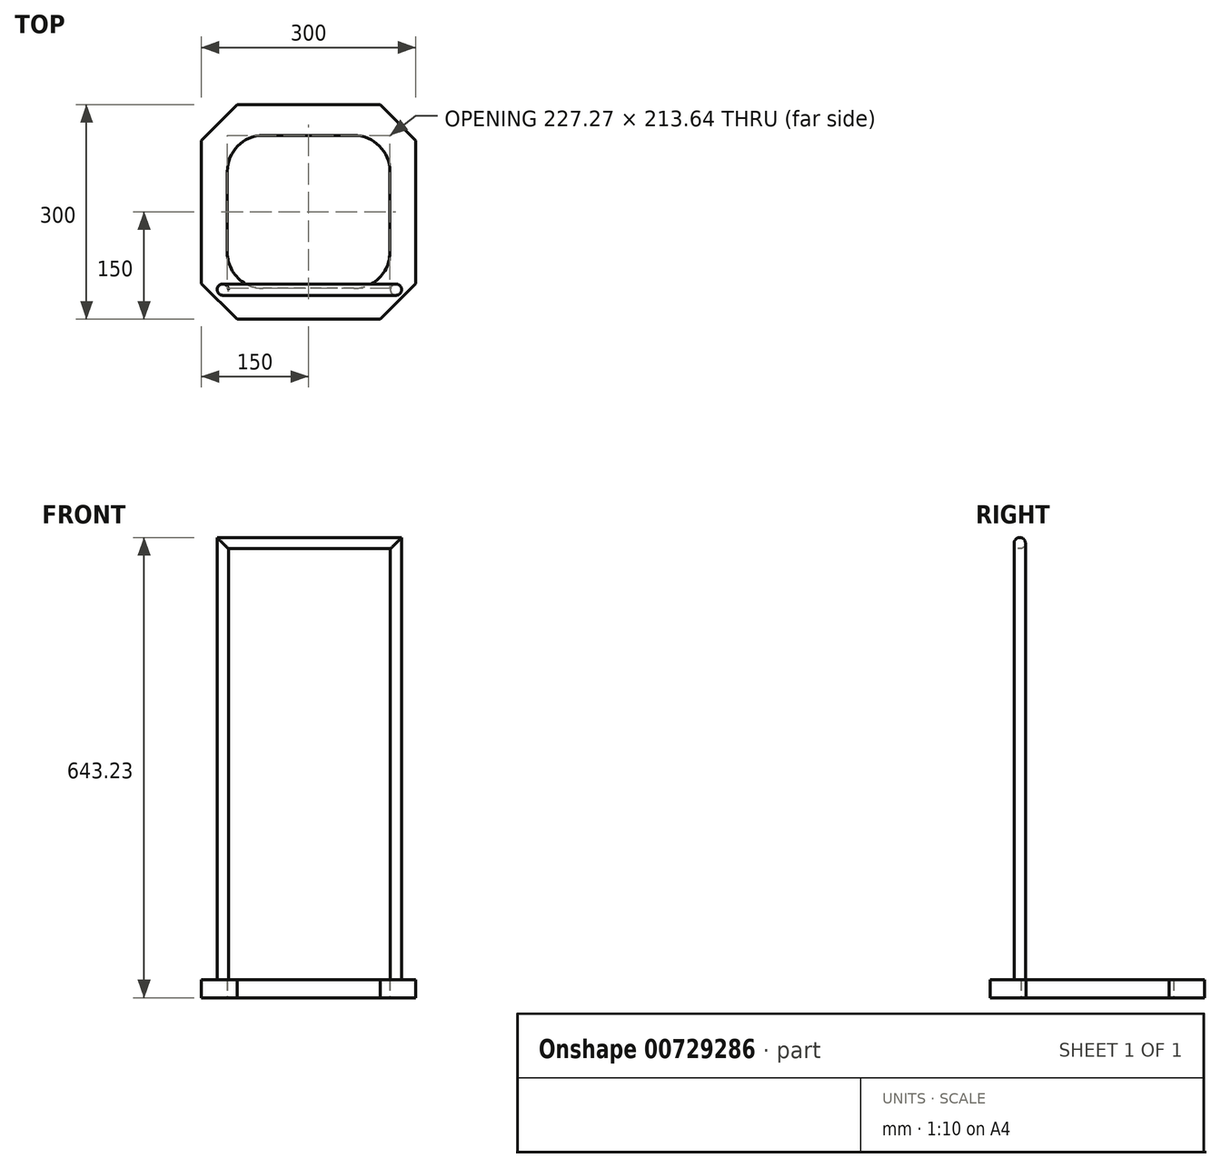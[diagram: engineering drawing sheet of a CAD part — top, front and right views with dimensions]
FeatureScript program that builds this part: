
annotation { "Feature Type Name" : "Feature", "Feature Type Description" : "" }
export const myFeature = defineFeature(function(context is Context, id is Id, definition is map)
    precondition{}
    {
        {
            var Q0;
            Q0=qCreatedBy(makeId("Top.planeOp"),FACE);
            var sketch = newSketch(context, id + "F0", { "sketchPlane" : qUnion([Q0])});
            skLineSegment(sketch, "E0.bottom", {"start": v(150, -150) * mm, "end": v(-150, -150) * mm});
            skLineSegment(sketch, "E0.top", {"start": v(150, 150) * mm, "end": v(-150, 150) * mm});
            skLineSegment(sketch, "E0.left", {"start": v(150, -150) * mm, "end": v(150, 150) * mm});
            skLineSegment(sketch, "E0.right", {"start": v(-150, -150) * mm, "end": v(-150, 150) * mm});
            skPoint(sketch, "E0.middle", {"position": v(0, 0) * mm});
            skLineSegment(sketch, "E1.bottom", {"start": v(113.64, -106.82) * mm, "end": v(-113.64, -106.82) * mm});
            skLineSegment(sketch, "E1.top", {"start": v(113.64, 106.82) * mm, "end": v(-113.64, 106.82) * mm});
            skLineSegment(sketch, "E1.left", {"start": v(113.64, -106.82) * mm, "end": v(113.64, 106.82) * mm});
            skLineSegment(sketch, "E1.right", {"start": v(-113.64, -106.82) * mm, "end": v(-113.64, 106.82) * mm});
            skSolve(sketch);
        }
        {
            var Q0;
            Q0 = qSketchRegion(id + "F0", true);
            extrude(context, id + "F1", {"entities" : qUnion([Q0]), "depth" : 25 * mm, "offsetDistance" : 25 * mm});
        }
        {
            var Q0;
            Q0=makeQuery(id+"F1.opExtrude","SWEPT_EDGE",EDGE,{"disambiguationData":[OSD([sQuery(id+"F0.wireOp",EDGE,"E1.bottom"),sQuery(id+"F0.wireOp",EDGE,"E1.right")])]});
            var Q1;
            Q1=makeQuery(id+"F1.opExtrude","SWEPT_EDGE",EDGE,{"disambiguationData":[OSD([sQuery(id+"F0.wireOp",EDGE,"E1.top"),sQuery(id+"F0.wireOp",EDGE,"E1.right")])]});
            var Q2;
            Q2=makeQuery(id+"F1.opExtrude","SWEPT_EDGE",EDGE,{"disambiguationData":[OSD([sQuery(id+"F0.wireOp",EDGE,"E1.bottom"),sQuery(id+"F0.wireOp",EDGE,"E1.left")])]});
            var Q3;
            Q3=makeQuery(id+"F1.opExtrude","SWEPT_EDGE",EDGE,{"disambiguationData":[OSD([sQuery(id+"F0.wireOp",EDGE,"E1.top"),sQuery(id+"F0.wireOp",EDGE,"E1.left")])]});
            fillet(context, id + "F2", {"entities" : qUnion([Q0, Q1, Q2, Q3]), "radius" : 50 * mm, "tangentPropagation" : true, "allowEdgeOverflow" : false});
        }
        {
            var Q0;
            Q0=makeQuery(id+"F1.opExtrude","SWEPT_EDGE",EDGE,{"disambiguationData":[OSD([sQuery(id+"F0.wireOp",EDGE,"E0.top"),sQuery(id+"F0.wireOp",EDGE,"E0.right")])]});
            var Q1;
            Q1=makeQuery(id+"F1.opExtrude","SWEPT_EDGE",EDGE,{"disambiguationData":[OSD([sQuery(id+"F0.wireOp",EDGE,"E0.top"),sQuery(id+"F0.wireOp",EDGE,"E0.left")])]});
            var Q2;
            Q2=makeQuery(id+"F1.opExtrude","SWEPT_EDGE",EDGE,{"disambiguationData":[OSD([sQuery(id+"F0.wireOp",EDGE,"E0.bottom"),sQuery(id+"F0.wireOp",EDGE,"E0.left")])]});
            var Q3;
            Q3=makeQuery(id+"F1.opExtrude","SWEPT_EDGE",EDGE,{"disambiguationData":[OSD([sQuery(id+"F0.wireOp",EDGE,"E0.bottom"),sQuery(id+"F0.wireOp",EDGE,"E0.right")])]});
            chamfer(context, id + "F3", {"entities" : qUnion([Q0, Q1, Q2, Q3]), "width" : 50 * mm, "tangentPropagation" : true});
        }
        {
            var Q0;
            Q0=makeQuery(id+"F1.opExtrude","SWEPT_FACE",FACE,{"disambiguationData":[OSD([sQuery(id+"F0.wireOp",EDGE,"E0.bottom")])]});
            cPlane(context, id + "F4", {"entities" : qUnion([Q0]), "cplaneType" : CPlaneType.OFFSET, "offset" : 35 * mm, "oppositeDirection" : true, "width" : 150 * mm, "height" : 150 * mm});
        }
        {
            var Q0;
            Q0=qCreatedBy(id+"F4.planeOp",FACE);
            var sketch = newSketch(context, id + "F5", { "sketchPlane" : qUnion([Q0])});
            skLineSegment(sketch, "E2", {"start": v(-124.5, 0) * mm, "end": v(-124.5, 639.9) * mm});
            skLineSegment(sketch, "E3", {"start": v(126.83, 0) * mm, "end": v(126.83, 639.9) * mm});
            skLineSegment(sketch, "E4", {"start": v(126.83, 639.9) * mm, "end": v(-124.5, 639.9) * mm});
            skSolve(sketch);
        }
        {
            var Q0;
            Q0=makeQuery(id+"F1.opExtrude","CAP_FACE",FACE,{"disambiguationData":[OSD([sQuery(id+"F0.wireOp",EDGE,"E0.bottom"),sQuery(id+"F0.wireOp",EDGE,"E0.top"),sQuery(id+"F0.wireOp",EDGE,"E0.left"),sQuery(id+"F0.wireOp",EDGE,"E0.right"),sQuery(id+"F0.wireOp",EDGE,"E1.bottom"),sQuery(id+"F0.wireOp",EDGE,"E1.top"),sQuery(id+"F0.wireOp",EDGE,"E1.left"),sQuery(id+"F0.wireOp",EDGE,"E1.right")])],"isStart":false});
            var sketch = newSketch(context, id + "F6", { "sketchPlane" : qUnion([Q0])});
            skCircle(sketch, "E5", {"center": v(122.28, -108.6) * mm, "radius": 7.88 * mm});
            skSolve(sketch);
        }
        {
            var Q0;
            {var subQ0=sQuery(id+"F6.wireOp",EDGE,"E5");var subQ1=sQuery(id+"F0.wireOp",EDGE,"E0.left");var subQ2=sQuery(id+"F0.wireOp",EDGE,"E0.bottom");var subQ3=makeQuery(id+"F3.opChamfer","BLEND_EDGE",EDGE,{"blendedFrom":[makeQuery(id+"F1.opExtrude","SWEPT_EDGE",EDGE,{"disambiguationData":[OSD([subQ2,subQ1])]}),makeQuery(id+"F1.opExtrude","CAP_FACE",FACE,{"disambiguationData":[OSD([subQ2,sQuery(id+"F0.wireOp",EDGE,"E0.top"),subQ1,sQuery(id+"F0.wireOp",EDGE,"E0.right"),sQuery(id+"F0.wireOp",EDGE,"E1.bottom"),sQuery(id+"F0.wireOp",EDGE,"E1.top"),sQuery(id+"F0.wireOp",EDGE,"E1.left"),sQuery(id+"F0.wireOp",EDGE,"E1.right")])],"isStart":false})],"blendedInto":[makeQuery(id+"F1.opExtrude","CAP_FACE",FACE,{"disambiguationData":[OSD([subQ2,sQuery(id+"F0.wireOp",EDGE,"E0.top"),subQ1,sQuery(id+"F0.wireOp",EDGE,"E0.right"),sQuery(id+"F0.wireOp",EDGE,"E1.bottom"),sQuery(id+"F0.wireOp",EDGE,"E1.top"),sQuery(id+"F0.wireOp",EDGE,"E1.left"),sQuery(id+"F0.wireOp",EDGE,"E1.right")])],"isStart":false})]});var subQ4=makeQuery(id+"F6.imprint","INTERSECT",VERTEX,{"disambiguationData":[OD(0.0)],"derivedFrom":[subQ3,subQ0]});Q0=makeQuery(id+"F6.imprint","IMPRINT",FACE,{"disambiguationData":[TD([[makeQuery(id+"F6.imprint","IMPRINT",EDGE,{"disambiguationData":[TD([[subQ4,-1.0]])],"derivedFrom":subQ0}),1.0]])]});}
            var Q1;
            {var subQ0=sQuery(id+"F6.wireOp",EDGE,"E5");var subQ1=sQuery(id+"F0.wireOp",EDGE,"E0.left");var subQ2=sQuery(id+"F0.wireOp",EDGE,"E0.bottom");var subQ3=makeQuery(id+"F3.opChamfer","BLEND_EDGE",EDGE,{"blendedFrom":[makeQuery(id+"F1.opExtrude","SWEPT_EDGE",EDGE,{"disambiguationData":[OSD([subQ2,subQ1])]}),makeQuery(id+"F1.opExtrude","CAP_FACE",FACE,{"disambiguationData":[OSD([subQ2,sQuery(id+"F0.wireOp",EDGE,"E0.top"),subQ1,sQuery(id+"F0.wireOp",EDGE,"E0.right"),sQuery(id+"F0.wireOp",EDGE,"E1.bottom"),sQuery(id+"F0.wireOp",EDGE,"E1.top"),sQuery(id+"F0.wireOp",EDGE,"E1.left"),sQuery(id+"F0.wireOp",EDGE,"E1.right")])],"isStart":false})],"blendedInto":[makeQuery(id+"F1.opExtrude","CAP_FACE",FACE,{"disambiguationData":[OSD([subQ2,sQuery(id+"F0.wireOp",EDGE,"E0.top"),subQ1,sQuery(id+"F0.wireOp",EDGE,"E0.right"),sQuery(id+"F0.wireOp",EDGE,"E1.bottom"),sQuery(id+"F0.wireOp",EDGE,"E1.top"),sQuery(id+"F0.wireOp",EDGE,"E1.left"),sQuery(id+"F0.wireOp",EDGE,"E1.right")])],"isStart":false})]});var subQ4=makeQuery(id+"F6.imprint","INTERSECT",VERTEX,{"disambiguationData":[OD(0.0)],"derivedFrom":[subQ3,subQ0]});Q1=makeQuery(id+"F6.imprint","IMPRINT",FACE,{"disambiguationData":[TD([[makeQuery(id+"F6.imprint","IMPRINT",EDGE,{"disambiguationData":[TD([[subQ4,1.0]])],"derivedFrom":subQ0}),1.0]])]});}
            var Q2;
            Q2=sQuery(id+"F5.wireOp",EDGE,"E3");
            var Q3;
            Q3=sQuery(id+"F5.wireOp",EDGE,"E4");
            var Q4;
            Q4=sQuery(id+"F5.wireOp",EDGE,"E2");
            sweep(context, id + "F7", {"operationType" : NewBodyOperationType.ADD, "profiles" : qUnion([Q0, Q1]), "path" : qUnion([Q2, Q3, Q4])});
        }
    });
